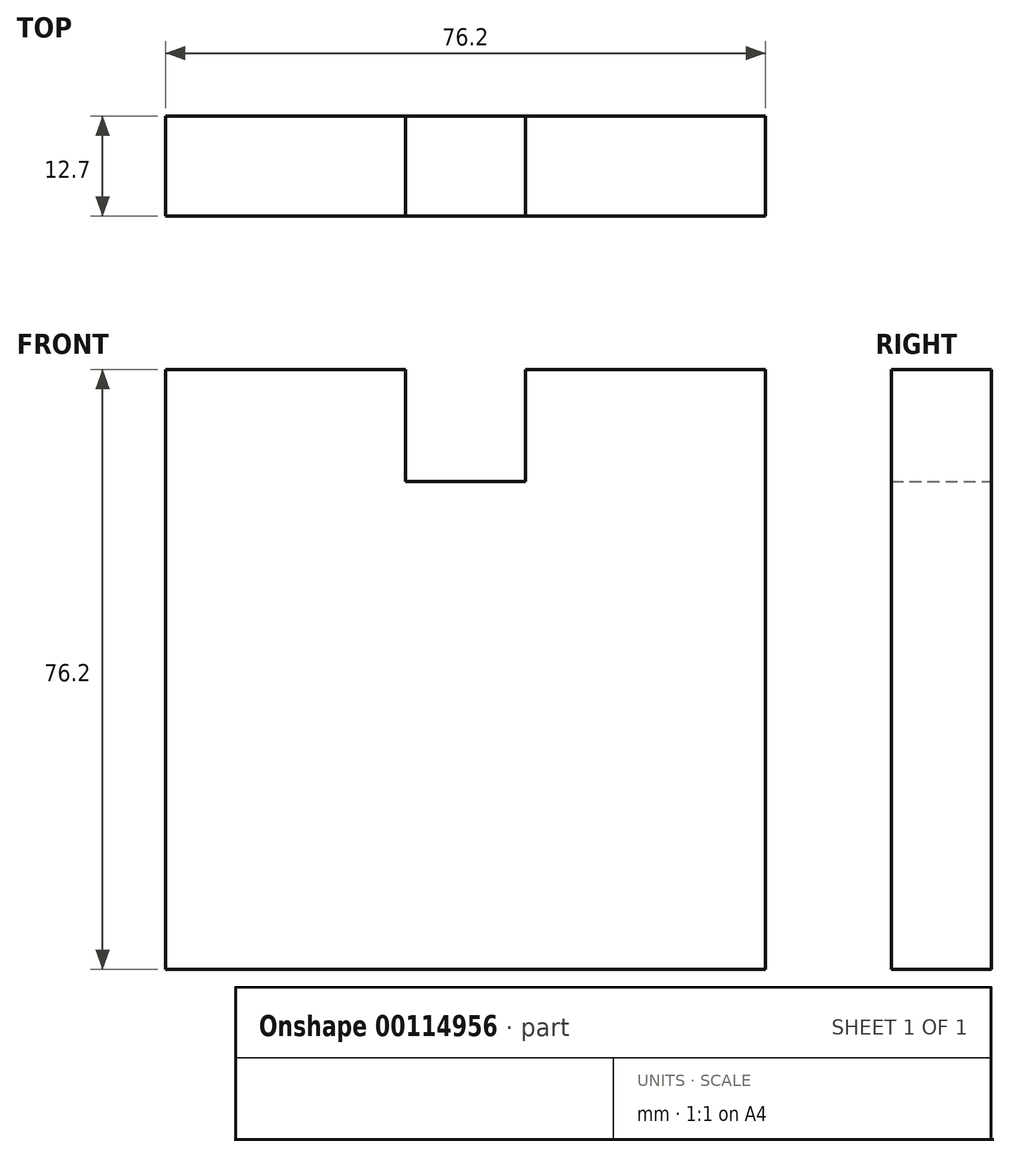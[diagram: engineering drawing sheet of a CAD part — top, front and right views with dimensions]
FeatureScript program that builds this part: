
annotation { "Feature Type Name" : "Feature", "Feature Type Description" : "" }
export const myFeature = defineFeature(function(context is Context, id is Id, definition is map)
    precondition{}
    {
        {
            var Q0;
            Q0=qCreatedBy(makeId("Front.planeOp"),FACE);
            var sketch = newSketch(context, id + "F0", { "sketchPlane" : qUnion([Q0])});
            skLineSegment(sketch, "E0", {"start": v(0, 0) * mm, "end": v(0, -76.2) * mm});
            skLineSegment(sketch, "E1", {"start": v(0, -76.2) * mm, "end": v(76.2, -76.2) * mm});
            skLineSegment(sketch, "E2", {"start": v(76.2, -76.2) * mm, "end": v(76.2, 0) * mm});
            skLineSegment(sketch, "E3", {"start": v(76.2, 0) * mm, "end": v(0, 0) * mm});
            skSolve(sketch);
        }
        {
            var Q0;
            Q0=makeQuery(id+"F0.imprint","IMPRINT",FACE,{"disambiguationData":[TD([[makeQuery(id+"F0.imprint","IMPRINT",EDGE,{"derivedFrom":sQuery(id+"F0.wireOp",EDGE,"E0")}),1.0]])]});
            extrude(context, id + "F1", {"entities" : qUnion([Q0]), "depth" : 12.7 * mm});
        }
        {
            var Q0;
            Q0=qCreatedBy(makeId("Front.planeOp"),FACE);
            var sketch = newSketch(context, id + "F2", { "sketchPlane" : qUnion([Q0])});
            skLineSegment(sketch, "E4", {"start": v(30.48, 0) * mm, "end": v(30.48, -14.22) * mm});
            skLineSegment(sketch, "E5", {"start": v(30.48, -14.22) * mm, "end": v(45.72, -14.22) * mm});
            skLineSegment(sketch, "E6", {"start": v(45.72, -14.22) * mm, "end": v(45.72, 0) * mm});
            skLineSegment(sketch, "E7", {"start": v(45.72, 0) * mm, "end": v(30.48, 0) * mm});
            skSolve(sketch);
        }
        {
            var Q0;
            Q0=makeQuery(id+"F2.imprint","IMPRINT",FACE,{"disambiguationData":[TD([[makeQuery(id+"F2.imprint","IMPRINT",EDGE,{"derivedFrom":sQuery(id+"F2.wireOp",EDGE,"E4")}),1.0]])]});
            extrude(context, id + "F3", {"entities" : qUnion([Q0]), "operationType" : NewBodyOperationType.REMOVE, "depth" : 25.4 * mm});
        }
    });
